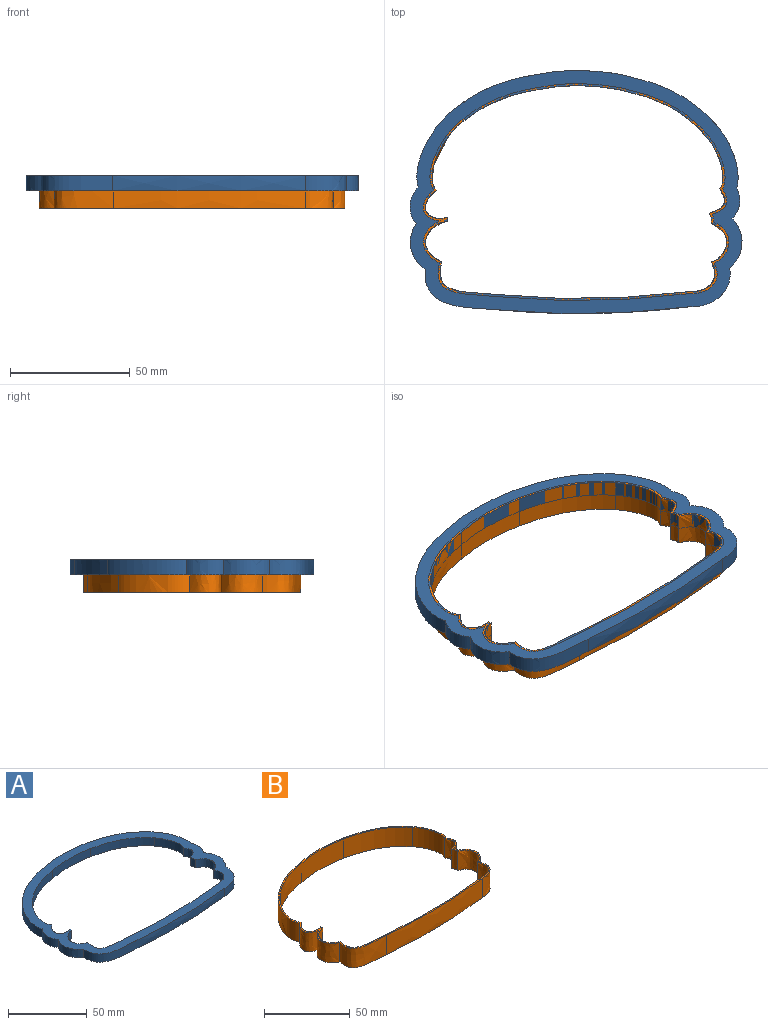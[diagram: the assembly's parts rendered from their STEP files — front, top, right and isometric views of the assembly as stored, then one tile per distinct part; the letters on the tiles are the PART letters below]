
ASSEMBLY  parts=2 mates=1
PART A: 28 faces, bbox 139.2x102.1x6.9 mm
  f0: plane 139.16x102.15mm, normal (0,0,1), area 2508.8mm2, adj f2,f3,f4,f5,f6,f7,f8,f9
  f1: plane 139.16x102.15mm, normal (0,0,-1), area 2508.8mm2, adj f2,f3,f4,f5,f6,f7,f8,f9
  f2: extruded ~33.19x16.61mm, area 246.1mm2, adj f0,f1,f3,f13
  f3: extruded ~15.44x6.35mm, area 107.4mm2, adj f0,f1,f2,f4
  f4: extruded ~19.11x6.35mm, area 137.9mm2, adj f0,f1,f3,f5
  f5: extruded ~29.92x16.76mm, area 249.9mm2, adj f0,f1,f4,f6
  f6: extruded ~80.62x6.35mm, area 513mm2, adj f0,f1,f5,f7
  f7: extruded ~16.9x15.93mm, area 168.7mm2, adj f0,f1,f6,f8
  f8: extruded ~20.94x6.35mm, area 149.7mm2, adj f0,f1,f7,f9
  f9: extruded ~12.8x6.35mm, area 88.5mm2, adj f0,f1,f8,f10
  f10: extruded ~24.77x7.85mm, area 168.9mm2, adj f0,f1,f9,f11
  f11: extruded ~40.42x22.46mm, area 300mm2, adj f0,f1,f10,f12
  f12: extruded ~36.44x6.35mm, area 233mm2, adj f0,f1,f11,f13
  f13: extruded ~32.84x13.62mm, area 228.4mm2, adj f0,f1,f2,f12
  f14: extruded ~29.3x13.83mm, area 217.6mm2, adj f0,f1,f15,f27
  f15: extruded ~11.94x9.41mm, area 131.7mm2, adj f0,f1,f14,f16
  f16: plane 6.35x1.75mm, normal (1,0,0), area 11.1mm2, adj f0,f1,f15,f17
  f17: extruded ~16.82x9.28mm, area 158.9mm2, adj f0,f1,f16,f18
  f18: extruded ~24.01x13.72mm, area 210.6mm2, adj f0,f1,f17,f19
  f19: extruded ~79.88x6.35mm, area 508.3mm2, adj f0,f1,f18,f20
  f20: extruded ~12.56x10.86mm, area 128.1mm2, adj f0,f1,f19,f21
  f21: extruded ~15.96x6.54mm, area 140.8mm2, adj f0,f1,f20,f22
  f22: extruded ~6.35x4.16mm, area 27.4mm2, adj f0,f1,f21,f23
  f23: extruded ~10.27x6.35mm, area 90.8mm2, adj f0,f1,f22,f24
  f24: extruded ~21.1x6.4mm, area 145.2mm2, adj f0,f1,f23,f25
  f25: extruded ~36.72x20.26mm, area 272.1mm2, adj f0,f1,f24,f26
  f26: extruded ~34.06x6.35mm, area 217.7mm2, adj f0,f1,f25,f27
  f27: extruded ~30.45x12.65mm, area 211.9mm2, adj f0,f1,f14,f26
PART B: 29 faces, bbox 133.4x94.2x17.2 mm
  f0: plane 133.35x94.16mm, normal (0,0,1), area 346.4mm2, adj f2,f3,f4,f5,f6,f7,f8,f9
  f1: plane 133.35x94.16mm, normal (0,0,-1), area 346.4mm2, adj f2,f3,f4,f5,f6,f7,f8,f9
  f2: extruded ~29.89x14.21mm, area 478.4mm2, adj f0,f1,f3,f14
  f3: extruded ~13.72x12.99mm, area 258.1mm2, adj f0,f1,f2,f4
  f4: extruded ~17.54x13.72mm, area 321.7mm2, adj f0,f1,f3,f5
  f5: extruded ~24.83x14.1mm, area 466.1mm2, adj f0,f1,f4,f6
  f6: extruded ~79.97x13.72mm, area 1099.3mm2, adj f0,f1,f5,f7
  f7: extruded ~13.72x12.79mm, area 284.6mm2, adj f0,f1,f6,f8
  f8: extruded ~17.17x13.72mm, area 308.9mm2, adj f0,f1,f7,f9
  f9: extruded ~13.72x3.16mm, area 44.4mm2, adj f0,f1,f8,f10
  f10: extruded ~13.72x10.71mm, area 196.8mm2, adj f0,f1,f9,f11
  f11: extruded ~21.67x13.72mm, area 321mm2, adj f0,f1,f10,f12
  f12: extruded ~37.24x20.57mm, area 596.1mm2, adj f0,f1,f11,f13
  f13: extruded ~34.39x13.72mm, area 474.9mm2, adj f0,f1,f12,f14
  f14: extruded ~30.78x13.72mm, area 462.6mm2, adj f0,f1,f2,f13
  f15: extruded ~29.3x13.83mm, area 469.9mm2, adj f0,f1,f16,f28
  f16: extruded ~13.72x11.94mm, area 284.4mm2, adj f0,f1,f15,f17
  f17: plane 13.72x1.75mm, normal (1,0,0), area 24mm2, adj f0,f1,f16,f18
  f18: extruded ~16.82x13.72mm, area 343.2mm2, adj f0,f1,f17,f19
  f19: extruded ~24.01x13.72mm, area 454.9mm2, adj f0,f1,f18,f20
  f20: extruded ~79.88x13.72mm, area 1098mm2, adj f0,f1,f19,f21
  f21: extruded ~13.72x12.56mm, area 276.7mm2, adj f0,f1,f20,f22
  f22: extruded ~15.96x13.72mm, area 304mm2, adj f0,f1,f21,f23
  f23: extruded ~13.72x4.16mm, area 59.1mm2, adj f0,f1,f22,f24
  f24: extruded ~13.72x10.27mm, area 196.1mm2, adj f0,f1,f23,f25
  f25: extruded ~21.1x13.72mm, area 313.6mm2, adj f0,f1,f24,f26
  f26: extruded ~36.72x20.26mm, area 587.7mm2, adj f0,f1,f25,f27
  f27: extruded ~34.06x13.72mm, area 470.3mm2, adj f0,f1,f26,f28
  f28: extruded ~30.45x13.72mm, area 457.8mm2, adj f0,f1,f15,f27
PLACE A t=(-22.76,11.02,7.37)mm
PLACE B t=(232.94,21.7,0)mm
MATE fastened A.f0 <-> B.f0  axis (0,0,1) through (174.04,12.23,13.72)mm
